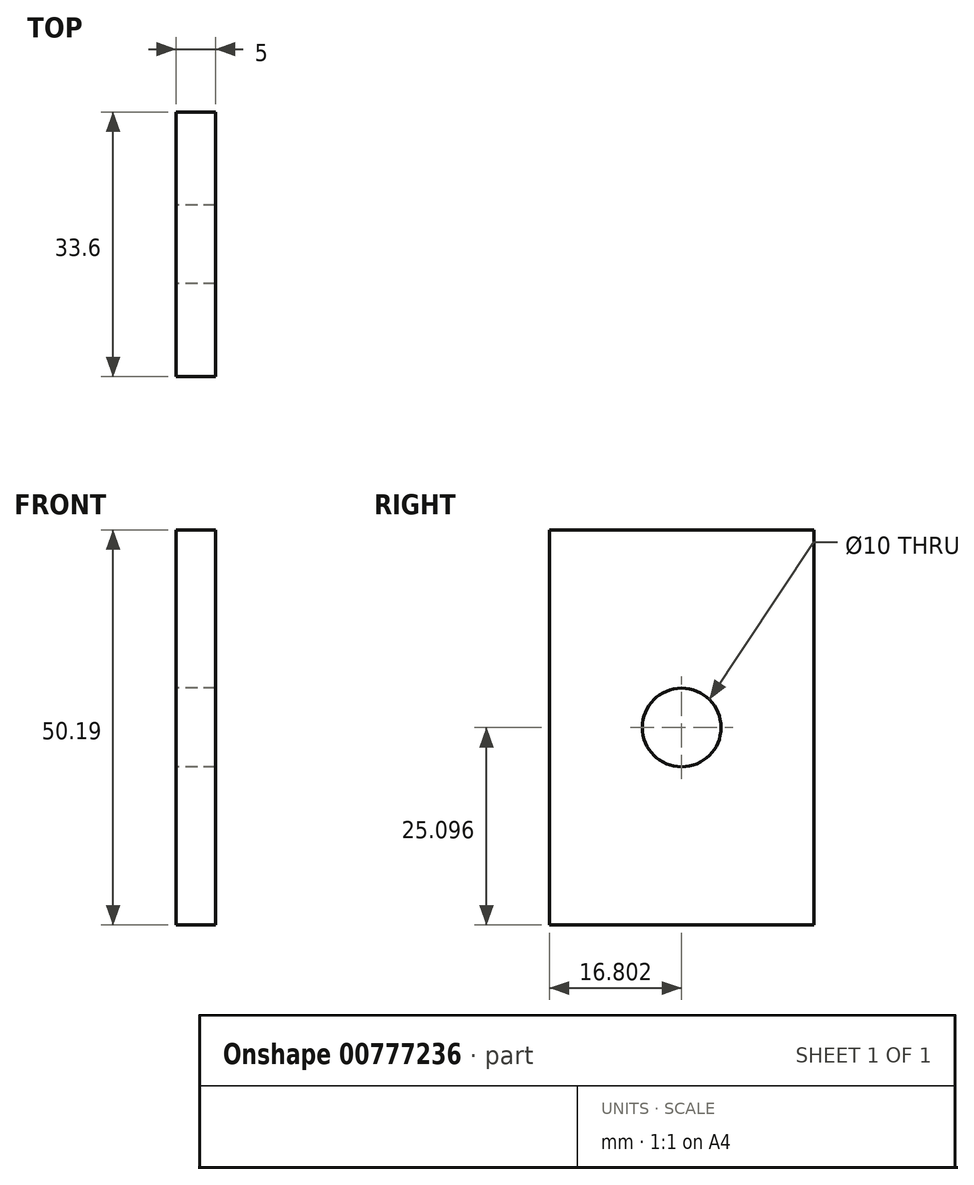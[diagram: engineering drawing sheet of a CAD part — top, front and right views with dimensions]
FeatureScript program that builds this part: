
annotation { "Feature Type Name" : "Feature", "Feature Type Description" : "" }
export const myFeature = defineFeature(function(context is Context, id is Id, definition is map)
    precondition{}
    {
        {
            var Q0;
            Q0=qCreatedBy(makeId("Right.planeOp"),FACE);
            var sketch = newSketch(context, id + "F0", { "sketchPlane" : qUnion([Q0])});
            skLineSegment(sketch, "E0.bottom", {"start": v(-27.44, 0) * mm, "end": v(-101.04, 0) * mm});
            skLineSegment(sketch, "E0.top", {"start": v(-27.44, 50.2) * mm, "end": v(-101.04, 50.2) * mm});
            skLineSegment(sketch, "E0.left", {"start": v(-27.44, 0) * mm, "end": v(-27.44, 50.2) * mm});
            skLineSegment(sketch, "E0.right", {"start": v(-101.04, 0) * mm, "end": v(-101.04, 50.2) * mm});
            skPoint(sketch, "E0.middle", {"position": v(-64.24, 25.1) * mm});
            skCircle(sketch, "E1", {"center": v(-64.24, 25.1) * mm, "radius": 5 * mm});
            skSolve(sketch);
        }
        {
            var Q0;
            Q0=makeQuery(id+"F0.imprint","IMPRINT",FACE,{"disambiguationData":[TD([[makeQuery(id+"F0.imprint","IMPRINT",EDGE,{"derivedFrom":sQuery(id+"F0.wireOp",EDGE,"E0.bottom")}),-1.0]])]});
            extrude(context, id + "F1", {"entities" : qUnion([Q0]), "depth" : 5 * mm, "offsetDistance" : 25 * mm});
        }
        {
            var Q0;
            Q0=makeQuery(id+"F1.opExtrude","CAP_FACE",FACE,{"disambiguationData":[OSD([sQuery(id+"F0.wireOp",EDGE,"E0.bottom"),sQuery(id+"F0.wireOp",EDGE,"E0.top"),sQuery(id+"F0.wireOp",EDGE,"E0.left"),sQuery(id+"F0.wireOp",EDGE,"E0.right"),sQuery(id+"F0.wireOp",EDGE,"E1")])],"isStart":true});
            var sketch = newSketch(context, id + "F2", { "sketchPlane" : qUnion([Q0])});
            skLineSegment(sketch, "E2", {"start": v(78.6, -71.66) * mm, "end": v(78.6, 50.2) * mm, "construction": true});
            skLineSegment(sketch, "E3", {"start": v(48.95, -69.06) * mm, "end": v(48.95, 50.2) * mm, "construction": true});
            skLineSegment(sketch, "E4", {"start": v(48.95, 50.2) * mm, "end": v(48.95, 0) * mm});
            skLineSegment(sketch, "E5", {"start": v(78.6, 50.2) * mm, "end": v(78.6, 0) * mm});
            skSolve(sketch);
        }
        {
            var Q0;
            Q0 = qSketchRegion(id + "F2", true);
            var Q1;
            Q1=makeQuery(id+"F1.opExtrude","SWEPT_FACE",FACE,{"disambiguationData":[OSD([sQuery(id+"F0.wireOp",EDGE,"E0.right")])]});
            extrude(context, id + "F3", {"entities" : qUnion([Q0, Q1]), "operationType" : NewBodyOperationType.REMOVE, "oppositeDirection" : true, "depth" : 20 * mm, "offsetDistance" : 25 * mm});
        }
        {
            var Q0;
            Q0=makeQuery(id+"F1.opExtrude","SWEPT_FACE",FACE,{"disambiguationData":[OSD([sQuery(id+"F0.wireOp",EDGE,"E0.left")])]});
            extrude(context, id + "F4", {"entities" : qUnion([Q0]), "operationType" : NewBodyOperationType.REMOVE, "oppositeDirection" : true, "depth" : 20 * mm, "offsetDistance" : 25 * mm});
        }
    });
